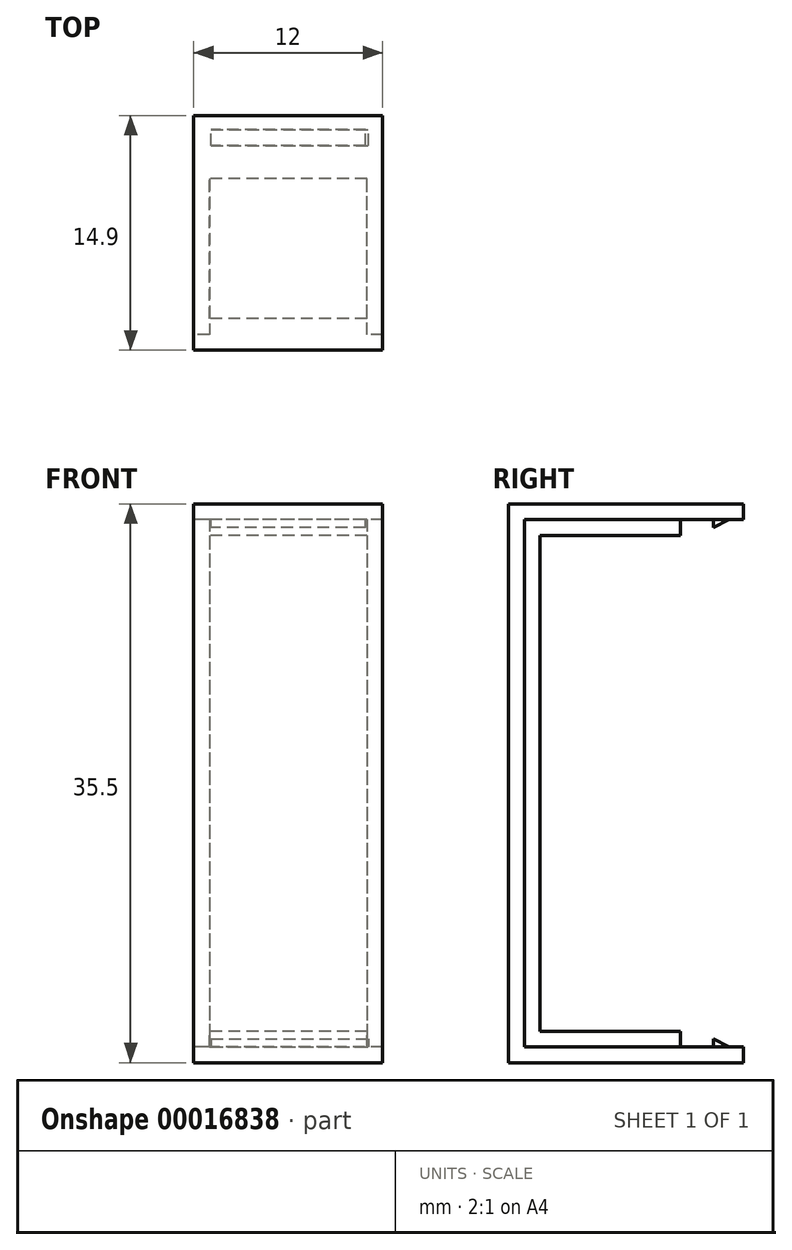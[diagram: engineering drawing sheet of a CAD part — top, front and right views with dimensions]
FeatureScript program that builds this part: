
annotation { "Feature Type Name" : "Feature", "Feature Type Description" : "" }
export const myFeature = defineFeature(function(context is Context, id is Id, definition is map)
    precondition{}
    {
        {
            var Q0;
            Q0=qCreatedBy(makeId("Front.planeOp"),FACE);
            var sketch = newSketch(context, id + "F0", { "sketchPlane" : qUnion([Q0])});
            skLineSegment(sketch, "E0.bottom", {"start": v(-59.34, 25.1) * mm, "end": v(-47.34, 25.1) * mm});
            skLineSegment(sketch, "E0.top", {"start": v(-59.34, -10.4) * mm, "end": v(-47.34, -10.4) * mm});
            skLineSegment(sketch, "E0.left", {"start": v(-59.34, 25.1) * mm, "end": v(-59.34, -10.4) * mm});
            skLineSegment(sketch, "E0.right", {"start": v(-47.34, 25.1) * mm, "end": v(-47.34, -10.4) * mm});
            skSolve(sketch);
        }
        {
            var Q0;
            Q0=makeQuery(id+"F0.imprint","IMPRINT",FACE,{"disambiguationData":[TD([[makeQuery(id+"F0.imprint","IMPRINT",EDGE,{"derivedFrom":sQuery(id+"F0.wireOp",EDGE,"E0.bottom")}),-1.0]])]});
            extrude(context, id + "F1", {"entities" : qUnion([Q0]), "depth" : 14.9 * mm});
        }
        {
            var Q0;
            Q0=makeQuery(id+"F1.opExtrude","CAP_FACE",FACE,{"disambiguationData":[OSD([sQuery(id+"F0.wireOp",EDGE,"E0.bottom"),sQuery(id+"F0.wireOp",EDGE,"E0.top"),sQuery(id+"F0.wireOp",EDGE,"E0.left"),sQuery(id+"F0.wireOp",EDGE,"E0.right")])],"isStart":true});
            var sketch = newSketch(context, id + "F2", { "sketchPlane" : qUnion([Q0])});
            skLineSegment(sketch, "E1.bottom", {"start": v(47.34, 23.1) * mm, "end": v(59.34, 23.1) * mm});
            skLineSegment(sketch, "E1.top", {"start": v(47.34, -8.4) * mm, "end": v(59.34, -8.4) * mm});
            skLineSegment(sketch, "E1.left", {"start": v(47.34, 23.1) * mm, "end": v(47.34, -8.4) * mm});
            skLineSegment(sketch, "E1.right", {"start": v(59.34, 23.1) * mm, "end": v(59.34, -8.4) * mm});
            skSolve(sketch);
        }
        {
            var Q0;
            Q0=makeQuery(id+"F2.imprint","IMPRINT",FACE,{"disambiguationData":[TD([[makeQuery(id+"F2.imprint","IMPRINT",EDGE,{"derivedFrom":sQuery(id+"F2.wireOp",EDGE,"E1.bottom")}),-1.0]])]});
            extrude(context, id + "F3", {"entities" : qUnion([Q0]), "operationType" : NewBodyOperationType.REMOVE, "oppositeDirection" : true, "depth" : 12.9 * mm});
        }
        {
            var Q0;
            Q0=makeQuery(id+"F3.boolean.opBoolean","COPY",FACE,{"derivedFrom":makeQuery(id+"F3.opExtrude","CAP_FACE",FACE,{"disambiguationData":[OSD([sQuery(id+"F2.wireOp",EDGE,"E1.bottom"),sQuery(id+"F2.wireOp",EDGE,"E1.top"),sQuery(id+"F2.wireOp",EDGE,"E1.left"),sQuery(id+"F2.wireOp",EDGE,"E1.right")])],"isStart":false})});
            var sketch = newSketch(context, id + "F4", { "sketchPlane" : qUnion([Q0])});
            skLineSegment(sketch, "E2.bottom", {"start": v(48.34, 23.1) * mm, "end": v(58.34, 23.1) * mm});
            skLineSegment(sketch, "E2.top", {"start": v(48.34, -8.4) * mm, "end": v(58.34, -8.4) * mm});
            skLineSegment(sketch, "E2.left", {"start": v(48.34, 23.1) * mm, "end": v(48.34, -8.4) * mm});
            skLineSegment(sketch, "E2.right", {"start": v(58.34, 23.1) * mm, "end": v(58.34, -8.4) * mm});
            skSolve(sketch);
        }
        {
            var Q0;
            {var subQ1=sQuery(id+"F4.wireOp",EDGE,"E2.left");Q0=makeQuery(id+"F4.imprint","IMPRINT",FACE,{"disambiguationData":[TD([[makeQuery(id+"F4.imprint","IMPRINT",EDGE,{"derivedFrom":subQ1}),-1.0]])]});}
            var Q1;
            {var subQ1=sQuery(id+"F4.wireOp",EDGE,"E2.right");Q1=makeQuery(id+"F4.imprint","IMPRINT",FACE,{"disambiguationData":[TD([[makeQuery(id+"F4.imprint","IMPRINT",EDGE,{"derivedFrom":subQ1}),1.0]])]});}
            extrude(context, id + "F5", {"entities" : qUnion([Q0, Q1]), "operationType" : NewBodyOperationType.REMOVE, "oppositeDirection" : true, "depth" : 1 * mm});
        }
        {
            var Q0;
            {var subQ0=sQuery(id+"F2.wireOp",EDGE,"E1.bottom");var subQ1=makeQuery(id+"F3.boolean.opBoolean","COPY",EDGE,{"derivedFrom":makeQuery(id+"F3.opExtrude","CAP_EDGE",EDGE,{"disambiguationData":[OSD([subQ0])],"isStart":false})});Q0=makeQuery(id+"F5.boolean.opBoolean","MERGE",FACE,{"derivedFrom":[makeQuery(id+"F3.boolean.opBoolean","COPY",FACE,{"derivedFrom":makeQuery(id+"F3.opExtrude","SWEPT_FACE",FACE,{"disambiguationData":[OSD([subQ0])]})}),makeQuery(id+"F5.opExtrude","SWEPT_FACE",FACE,{"disambiguationData":[OSD([subQ0]),TDD([makeQuery(id+"F4.imprint","IMPRINT",EDGE,{"disambiguationData":[TD([[makeQuery(id+"F4.imprint","INTERSECT",VERTEX,{"derivedFrom":[subQ1,makeQuery(id+"F3.boolean.opBoolean","COPY",EDGE,{"derivedFrom":makeQuery(id+"F3.opExtrude","CAP_EDGE",EDGE,{"disambiguationData":[OSD([sQuery(id+"F2.wireOp",EDGE,"E1.left")])],"isStart":false})})]}),-1.0]])],"derivedFrom":subQ1})])]}),makeQuery(id+"F5.opExtrude","SWEPT_FACE",FACE,{"disambiguationData":[OSD([subQ0]),TDD([makeQuery(id+"F4.imprint","IMPRINT",EDGE,{"disambiguationData":[TD([[makeQuery(id+"F4.imprint","INTERSECT",VERTEX,{"derivedFrom":[subQ1,makeQuery(id+"F3.boolean.opBoolean","COPY",EDGE,{"derivedFrom":makeQuery(id+"F3.opExtrude","CAP_EDGE",EDGE,{"disambiguationData":[OSD([sQuery(id+"F2.wireOp",EDGE,"E1.right")])],"isStart":false})})]}),1.0]])],"derivedFrom":subQ1})])]})]});}
            var sketch = newSketch(context, id + "F6", { "sketchPlane" : qUnion([Q0])});
            skLineSegment(sketch, "E3.bottom", {"start": v(-48.34, 12.9) * mm, "end": v(-58.34, 12.9) * mm});
            skLineSegment(sketch, "E3.top", {"start": v(-48.34, 4) * mm, "end": v(-58.34, 4) * mm});
            skLineSegment(sketch, "E3.left", {"start": v(-48.34, 12.9) * mm, "end": v(-48.34, 4) * mm});
            skLineSegment(sketch, "E3.right", {"start": v(-58.34, 12.9) * mm, "end": v(-58.34, 4) * mm});
            skSolve(sketch);
        }
        {
            var Q0;
            Q0=makeQuery(id+"F6.imprint","IMPRINT",FACE,{"disambiguationData":[TD([[makeQuery(id+"F6.imprint","IMPRINT",EDGE,{"derivedFrom":sQuery(id+"F6.wireOp",EDGE,"E3.top")}),1.0]])]});
            extrude(context, id + "F7", {"entities" : qUnion([Q0]), "operationType" : NewBodyOperationType.REMOVE, "oppositeDirection" : true, "depth" : 1 * mm});
        }
        {
            var Q0;
            {var subQ0=sQuery(id+"F2.wireOp",EDGE,"E1.top");var subQ1=makeQuery(id+"F3.boolean.opBoolean","COPY",EDGE,{"derivedFrom":makeQuery(id+"F3.opExtrude","CAP_EDGE",EDGE,{"disambiguationData":[OSD([subQ0])],"isStart":false})});Q0=makeQuery(id+"F5.boolean.opBoolean","MERGE",FACE,{"derivedFrom":[makeQuery(id+"F3.boolean.opBoolean","COPY",FACE,{"derivedFrom":makeQuery(id+"F3.opExtrude","SWEPT_FACE",FACE,{"disambiguationData":[OSD([subQ0])]})}),makeQuery(id+"F5.opExtrude","SWEPT_FACE",FACE,{"disambiguationData":[OSD([subQ0]),TDD([makeQuery(id+"F4.imprint","IMPRINT",EDGE,{"disambiguationData":[TD([[makeQuery(id+"F4.imprint","INTERSECT",VERTEX,{"derivedFrom":[subQ1,makeQuery(id+"F3.boolean.opBoolean","COPY",EDGE,{"derivedFrom":makeQuery(id+"F3.opExtrude","CAP_EDGE",EDGE,{"disambiguationData":[OSD([sQuery(id+"F2.wireOp",EDGE,"E1.left")])],"isStart":false})})]}),-1.0]])],"derivedFrom":subQ1})])]}),makeQuery(id+"F5.opExtrude","SWEPT_FACE",FACE,{"disambiguationData":[OSD([subQ0]),TDD([makeQuery(id+"F4.imprint","IMPRINT",EDGE,{"disambiguationData":[TD([[makeQuery(id+"F4.imprint","INTERSECT",VERTEX,{"derivedFrom":[subQ1,makeQuery(id+"F3.boolean.opBoolean","COPY",EDGE,{"derivedFrom":makeQuery(id+"F3.opExtrude","CAP_EDGE",EDGE,{"disambiguationData":[OSD([sQuery(id+"F2.wireOp",EDGE,"E1.right")])],"isStart":false})})]}),1.0]])],"derivedFrom":subQ1})])]})]});}
            var sketch = newSketch(context, id + "F8", { "sketchPlane" : qUnion([Q0])});
            skLineSegment(sketch, "E4.bottom", {"start": v(-58.34, -4) * mm, "end": v(-48.34, -4) * mm});
            skLineSegment(sketch, "E4.top", {"start": v(-58.34, -12.9) * mm, "end": v(-48.34, -12.9) * mm});
            skLineSegment(sketch, "E4.left", {"start": v(-58.34, -4) * mm, "end": v(-58.34, -12.9) * mm});
            skLineSegment(sketch, "E4.right", {"start": v(-48.34, -4) * mm, "end": v(-48.34, -12.9) * mm});
            skSolve(sketch);
        }
        {
            var Q0;
            Q0=makeQuery(id+"F8.imprint","IMPRINT",FACE,{"disambiguationData":[TD([[makeQuery(id+"F8.imprint","IMPRINT",EDGE,{"derivedFrom":sQuery(id+"F8.wireOp",EDGE,"E4.bottom")}),1.0]])]});
            extrude(context, id + "F9", {"entities" : qUnion([Q0]), "operationType" : NewBodyOperationType.REMOVE, "oppositeDirection" : true, "depth" : 1 * mm});
        }
        {
            var Q0;
            Q0=makeQuery(id+"F9.boolean.opBoolean","COPY",FACE,{"derivedFrom":makeQuery(id+"F9.opExtrude","CAP_FACE",FACE,{"disambiguationData":[OSD([sQuery(id+"F0.wireOp",EDGE,"E0.left"),sQuery(id+"F0.wireOp",EDGE,"E0.right"),sQuery(id+"F2.wireOp",EDGE,"E1.top"),sQuery(id+"F2.wireOp",EDGE,"E1.left"),sQuery(id+"F2.wireOp",EDGE,"E1.right"),sQuery(id+"F4.wireOp",EDGE,"E2.top"),sQuery(id+"F4.wireOp",EDGE,"E2.left"),sQuery(id+"F4.wireOp",EDGE,"E2.right"),sQuery(id+"F8.wireOp",EDGE,"E4.bottom"),sQuery(id+"F8.wireOp",EDGE,"E4.left"),sQuery(id+"F8.wireOp",EDGE,"E4.right")])],"isStart":false})});
            var sketch = newSketch(context, id + "F10", { "sketchPlane" : qUnion([Q0])});
            skLineSegment(sketch, "E5.bottom", {"start": v(-58.24, -1.9) * mm, "end": v(-48.24, -1.9) * mm});
            skLineSegment(sketch, "E5.top", {"start": v(-58.24, -0.9) * mm, "end": v(-48.24, -0.9) * mm});
            skLineSegment(sketch, "E5.left", {"start": v(-58.24, -1.9) * mm, "end": v(-58.24, -0.9) * mm});
            skLineSegment(sketch, "E5.right", {"start": v(-48.24, -1.9) * mm, "end": v(-48.24, -0.9) * mm});
            skSolve(sketch);
        }
        {
            var Q0;
            Q0=makeQuery(id+"F10.imprint","IMPRINT",FACE,{"disambiguationData":[TD([[makeQuery(id+"F10.imprint","IMPRINT",EDGE,{"derivedFrom":sQuery(id+"F10.wireOp",EDGE,"E5.bottom")}),1.0]])]});
            extrude(context, id + "F11", {"entities" : qUnion([Q0]), "operationType" : NewBodyOperationType.ADD, "depth" : 0.5 * mm});
        }
        {
            var Q0;
            Q0=makeQuery(id+"F11.opExtrude","CAP_EDGE",EDGE,{"disambiguationData":[OSD([sQuery(id+"F10.wireOp",EDGE,"E5.top")])],"isStart":false});
            chamfer(context, id + "F12", {"entities" : qUnion([Q0]), "chamferType" : ChamferType.TWO_OFFSETS, "width1" : 0.5 * mm, "oppositeDirection" : false, "width2" : 1 * mm, "tangentPropagation" : true});
        }
        {
            var Q0;
            Q0=makeQuery(id+"F7.boolean.opBoolean","COPY",FACE,{"derivedFrom":makeQuery(id+"F7.opExtrude","CAP_FACE",FACE,{"disambiguationData":[OSD([sQuery(id+"F0.wireOp",EDGE,"E0.left"),sQuery(id+"F0.wireOp",EDGE,"E0.right"),sQuery(id+"F2.wireOp",EDGE,"E1.bottom"),sQuery(id+"F2.wireOp",EDGE,"E1.left"),sQuery(id+"F2.wireOp",EDGE,"E1.right"),sQuery(id+"F4.wireOp",EDGE,"E2.bottom"),sQuery(id+"F4.wireOp",EDGE,"E2.left"),sQuery(id+"F4.wireOp",EDGE,"E2.right"),sQuery(id+"F6.wireOp",EDGE,"E3.top"),sQuery(id+"F6.wireOp",EDGE,"E3.left"),sQuery(id+"F6.wireOp",EDGE,"E3.right")])],"isStart":false})});
            var sketch = newSketch(context, id + "F13", { "sketchPlane" : qUnion([Q0])});
            skLineSegment(sketch, "E6.bottom", {"start": v(-48.44, 1.9) * mm, "end": v(-58.24, 1.9) * mm});
            skLineSegment(sketch, "E6.top", {"start": v(-48.44, 0.9) * mm, "end": v(-58.24, 0.9) * mm});
            skLineSegment(sketch, "E6.left", {"start": v(-48.44, 1.9) * mm, "end": v(-48.44, 0.9) * mm});
            skLineSegment(sketch, "E6.right", {"start": v(-58.24, 1.9) * mm, "end": v(-58.24, 0.9) * mm});
            skSolve(sketch);
        }
        {
            var Q0;
            Q0=makeQuery(id+"F13.imprint","IMPRINT",FACE,{"disambiguationData":[TD([[makeQuery(id+"F13.imprint","IMPRINT",EDGE,{"derivedFrom":sQuery(id+"F13.wireOp",EDGE,"E6.bottom")}),1.0]])]});
            extrude(context, id + "F14", {"entities" : qUnion([Q0]), "operationType" : NewBodyOperationType.ADD, "depth" : 0.5 * mm});
        }
        {
            var Q0;
            Q0=makeQuery(id+"F14.opExtrude","CAP_EDGE",EDGE,{"disambiguationData":[OSD([sQuery(id+"F13.wireOp",EDGE,"E6.top")])],"isStart":false});
            chamfer(context, id + "F15", {"entities" : qUnion([Q0]), "chamferType" : ChamferType.TWO_OFFSETS, "width1" : 0.5 * mm, "oppositeDirection" : false, "width2" : 1 * mm, "tangentPropagation" : true});
        }
    });
